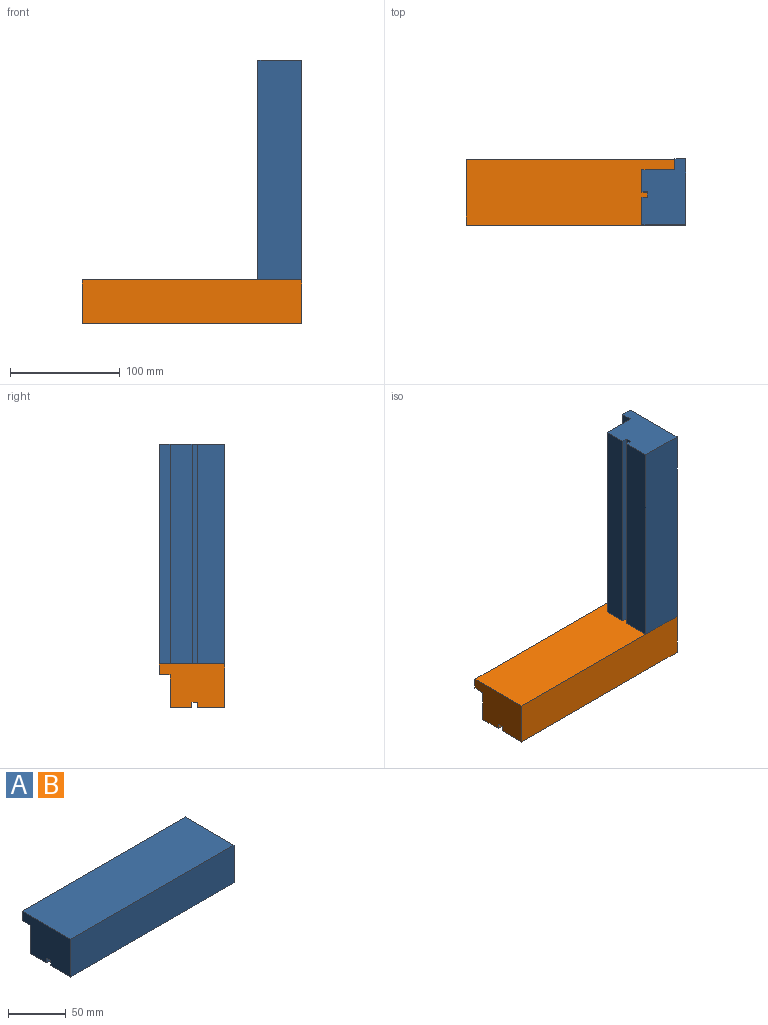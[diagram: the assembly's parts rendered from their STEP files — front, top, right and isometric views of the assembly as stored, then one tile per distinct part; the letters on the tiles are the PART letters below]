
ASSEMBLY  parts=2 mates=1
PART A: 12 faces, bbox 200x60x40 mm
  f0: plane 200x20mm, normal (0,0,-1), area 4000mm2, adj f1,f3,f8,f10
  f1: plane 60x40mm, normal (1,0,0), area 2075mm2, adj f0,f2,f3,f4,f5,f6,f7,f9
  f2: plane 200x25mm, normal (0,0,-1), area 5000mm2, adj f1,f7,f8,f9
  f3: plane 200x30mm, normal (0,1,0), area 6000mm2, adj f0,f1,f4,f8
  f4: plane 200x10mm, normal (0,0,-1), area 2000mm2, adj f1,f3,f5,f8
  f5: plane 200x10mm, normal (0,1,0), area 2000mm2, adj f1,f4,f6,f8
  f6: plane 200x60mm, normal (0,0,1), area 12000mm2, adj f1,f5,f7,f8
  f7: plane 200x40mm, normal (0,-1,0), area 8000mm2, adj f1,f2,f6,f8
  f8: plane 60x40mm, normal (-1,0,0), area 2075mm2, adj f0,f2,f3,f4,f5,f6,f7,f9
  f9: plane 200x5mm, normal (0,1,0), area 1000mm2, adj f1,f2,f8,f11
  f10: plane 200x5mm, normal (0,-1,0), area 1000mm2, adj f0,f1,f8,f11
  f11: plane 200x5mm, normal (0,0,-1), area 1000mm2, adj f1,f8,f9,f10
PART B: same geometry as A
PLACE A rot(axis=(0,1,0),90deg) t=(62.63,-49.31,48.28)mm
PLACE B t=(102.63,-49.31,8.28)mm
MATE slider A.f7 <-> B.f7  axis (0,-1,0) through (102.63,-99.31,48.28)mm
